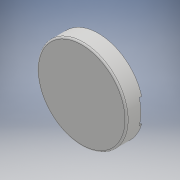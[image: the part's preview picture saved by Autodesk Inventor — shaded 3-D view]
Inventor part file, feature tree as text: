
AUTODESK INVENTOR PART (.ipt)
format: ipt  version: 2018 (Build 220112000, 112)  size: 245,760 bytes
history: native  units: mm
features: extrude x6, sketch x6, fillet x2, pattern_circular x1
ambient origin geometry x8: Origin, YZ Plane, XZ Plane, XY Plane, X Axis, Y Axis, Z Axis, Center Point
bodies: Solid1 (feature_tree)
feature tree (15):
  extrude  "Extrusion1"  Depth=0.4mm
  extrude  "Extrusion2"  Depth=10.0mm
  extrude  "Extrusion3"  Depth=27.25mm
  fillet  "Fillet1"  Radius=22.514747mm
  pattern_circular  "Circular Pattern1"  [2 undecoded]
  extrude  "Extrusion4"  Depth=1.6mm TaperAngle=0.0deg
  extrude  "Extrusion7"  Depth=0.5mm
  extrude  "Extrusion9"  Depth=1.6mm TaperAngle=360.0deg
  fillet  "Fillet5"  Radius=7.5mm
  sketch  "Sketch1"  dims[d2=0.4mm d3=0.0mm d4=54.5mm]
  sketch  "Sketch2"  dims[d5=10.0mm d6=0.0mm d7=56.0mm]
  sketch  "Sketch3"  dims[d8=56.0mm d9=27.25mm d10=22.514747mm]
  sketch  "Sketch4"  dims[d11=0.698132mm]
  sketch  "Sketch7"  dims[d12=26.25mm]
  sketch  "Sketch9"  dims[d13=22.514747mm d14=0.698132mm d15=1.4mm d16=0.0mm d17=0.5mm d18=20.0mm d19=360.0deg d25=7.5mm d26=3.0mm d27=7.5mm d28=3.0mm d29=1.5mm d30=0.0mm d47=48.0mm d48=6.5mm d49=0.0mm d50=54.5mm d51=3.0mm d52=7.5mm d53=3.0mm d54=7.5mm d55=1.0mm d56=0.5mm d60=36.0mm d61=1.6mm d62=0.0mm]
note: 2 required parameter values undecoded (feature->parameter linkage not recoverable at this tier; creation-order binding heuristic only, values carry confidence <= 0.55)
